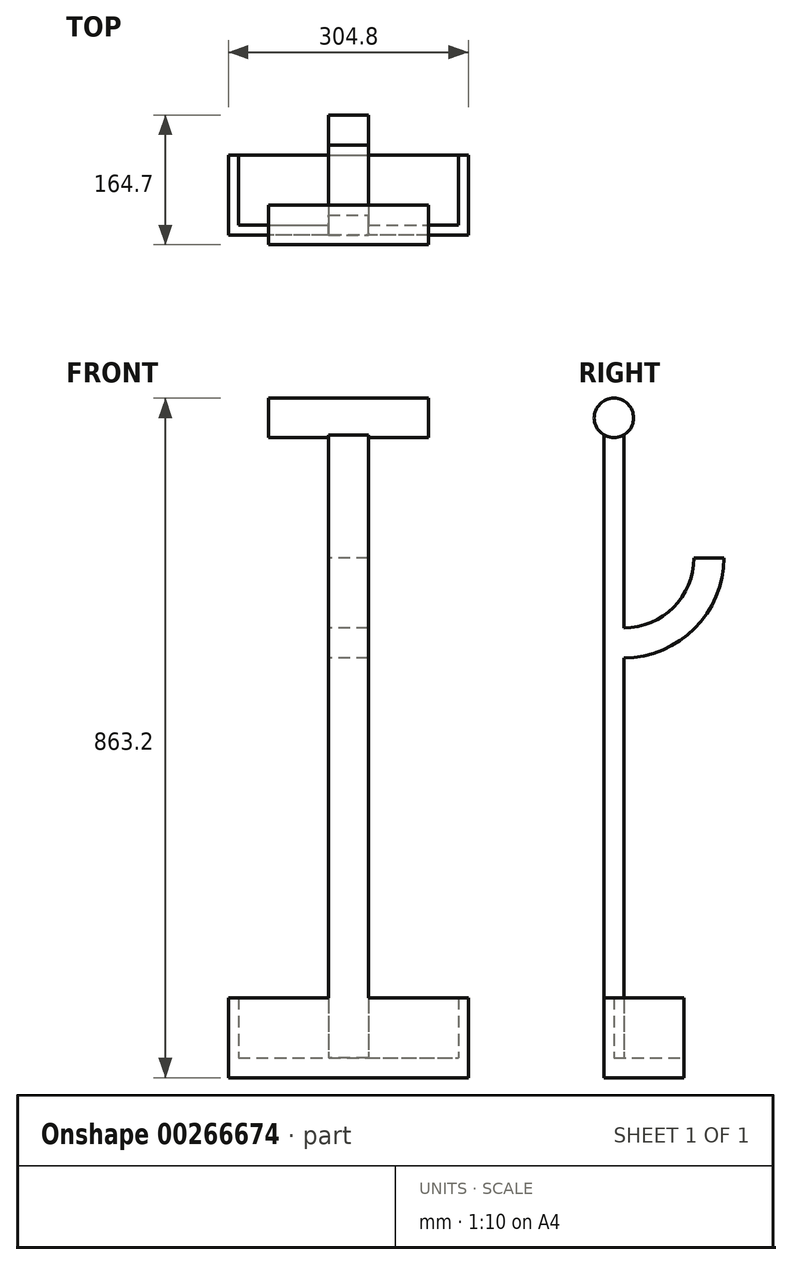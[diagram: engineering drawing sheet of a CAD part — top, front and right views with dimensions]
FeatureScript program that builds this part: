
annotation { "Feature Type Name" : "Feature", "Feature Type Description" : "" }
export const myFeature = defineFeature(function(context is Context, id is Id, definition is map)
    precondition{}
    {
        {
            var Q0;
            Q0=qCreatedBy(makeId("Top.planeOp"),FACE);
            var sketch = newSketch(context, id + "F0", { "sketchPlane" : qUnion([Q0])});
            skLineSegment(sketch, "E0", {"start": v(0, 0) * mm, "end": v(-152.4, 0) * mm});
            skLineSegment(sketch, "E1", {"start": v(-152.4, 0) * mm, "end": v(-152.4, 101.6) * mm});
            skLineSegment(sketch, "E2", {"start": v(-152.4, 101.6) * mm, "end": v(152.4, 101.6) * mm});
            skLineSegment(sketch, "E3", {"start": v(152.4, 101.6) * mm, "end": v(152.4, 0) * mm});
            skLineSegment(sketch, "E4", {"start": v(152.4, 0) * mm, "end": v(0, 0) * mm});
            skLineSegment(sketch, "E5", {"start": v(25.4, 0) * mm, "end": v(25.4, 25.4) * mm});
            skLineSegment(sketch, "E6", {"start": v(25.4, 25.4) * mm, "end": v(-25.4, 25.4) * mm});
            skLineSegment(sketch, "E7", {"start": v(-25.4, 25.4) * mm, "end": v(-25.4, 0) * mm});
            skLineSegment(sketch, "E8", {"start": v(-139.7, 101.6) * mm, "end": v(-139.7, 12.7) * mm});
            skLineSegment(sketch, "E9", {"start": v(-139.7, 12.7) * mm, "end": v(-25.4, 12.7) * mm});
            skLineSegment(sketch, "E10", {"start": v(25.4, 12.7) * mm, "end": v(139.7, 12.7) * mm});
            skLineSegment(sketch, "E11", {"start": v(139.7, 12.7) * mm, "end": v(139.7, 101.6) * mm});
            skSolve(sketch);
        }
        {
            var Q0;
            {var subQ1=sQuery(id+"F0.wireOp",EDGE,"E6");Q0=makeQuery(id+"F0.imprint","IMPRINT",FACE,{"disambiguationData":[TD([[makeQuery(id+"F0.imprint","IMPRINT",EDGE,{"derivedFrom":subQ1}),-1.0]])]});}
            extrude(context, id + "F1", {"entities" : qUnion([Q0]), "depth" : 25.4 * mm});
        }
        {
            var Q0;
            {var subQ5=sQuery(id+"F0.wireOp",EDGE,"E1");Q0=makeQuery(id+"F0.imprint","IMPRINT",FACE,{"disambiguationData":[TD([[makeQuery(id+"F0.imprint","IMPRINT",EDGE,{"derivedFrom":subQ5}),-1.0]])]});}
            var Q1;
            {var subQ4=sQuery(id+"F0.wireOp",EDGE,"E3");Q1=makeQuery(id+"F0.imprint","IMPRINT",FACE,{"disambiguationData":[TD([[makeQuery(id+"F0.imprint","IMPRINT",EDGE,{"derivedFrom":subQ4}),-1.0]])]});}
            extrude(context, id + "F2", {"entities" : qUnion([Q0, Q1]), "operationType" : NewBodyOperationType.ADD, "depth" : 101.6 * mm});
        }
        {
            var Q0;
            {var subQ0=sQuery(id+"F0.wireOp",EDGE,"E6");Q0=makeQuery(id+"F0.imprint","IMPRINT",FACE,{"disambiguationData":[TD([[makeQuery(id+"F0.imprint","IMPRINT",EDGE,{"derivedFrom":subQ0}),1.0]])]});}
            extrude(context, id + "F3", {"entities" : qUnion([Q0]), "operationType" : NewBodyOperationType.ADD, "depth" : 838.2 * mm});
        }
        {
            var Q0;
            Q0=makeQuery(id+"F3.opExtrude","SWEPT_FACE",FACE,{"disambiguationData":[OSD([sQuery(id+"F0.wireOp",EDGE,"E7")])]});
            var sketch = newSketch(context, id + "F4", { "sketchPlane" : qUnion([Q0])});
            skCircle(sketch, "E12", {"center": v(-12.7, 838.2) * mm, "radius": 25 * mm});
            skArc(sketch, "E13", {"start": v(-114.3, 660.4) * mm, "mid": v(-88.26, 597.54) * mm, "end": v(-25.4, 571.5) * mm});
            skPoint(sketch, "E14", {"position": v(-25.4, 838.2) * mm});
            skArc(sketch, "E15.0", {"start": v(-152.4, 660.4) * mm, "mid": v(-115.2, 570.6) * mm, "end": v(-25.4, 533.4) * mm});
            skLineSegment(sketch, "E16", {"start": v(-152.4, 660.4) * mm, "end": v(-114.3, 660.4) * mm});
            skLineSegment(sketch, "E17", {"start": v(-114.3, 660.4) * mm, "end": v(-25.4, 660.4) * mm, "construction": true});
            skSolve(sketch);
        }
        {
            var Q0;
            {var subQ0=sQuery(id+"F4.wireOp",EDGE,"E13");Q0=makeQuery(id+"F4.imprint","IMPRINT",FACE,{"disambiguationData":[TD([[makeQuery(id+"F4.imprint","IMPRINT",EDGE,{"derivedFrom":subQ0}),-1.0]])]});}
            extrude(context, id + "F5", {"entities" : qUnion([Q0]), "operationType" : NewBodyOperationType.ADD, "oppositeDirection" : true, "depth" : 50.8 * mm});
        }
        {
            var Q0;
            {var subQ1=sQuery(id+"F0.wireOp",EDGE,"E7");var subQ6=makeQuery(id+"F3.opExtrude","CAP_EDGE",EDGE,{"disambiguationData":[OSD([subQ1])],"isStart":false});Q0=makeQuery(id+"F4.imprint","IMPRINT",FACE,{"disambiguationData":[TD([[makeQuery(id+"F4.imprint","IMPRINT",EDGE,{"derivedFrom":subQ6}),1.0]])]});}
            var Q1;
            {var subQ1=sQuery(id+"F0.wireOp",EDGE,"E7");var subQ6=makeQuery(id+"F3.opExtrude","CAP_EDGE",EDGE,{"disambiguationData":[OSD([subQ1])],"isStart":false});Q1=makeQuery(id+"F4.imprint","IMPRINT",FACE,{"disambiguationData":[TD([[makeQuery(id+"F4.imprint","IMPRINT",EDGE,{"derivedFrom":subQ6}),-1.0]])]});}
            extrude(context, id + "F6", {"entities" : qUnion([Q0, Q1]), "depth" : 76.2 * mm});
        }
        {
            var Q0;
            Q0=makeQuery(id+"F6.opExtrude","CAP_FACE",FACE,{"disambiguationData":[OSD([sQuery(id+"F0.wireOp",EDGE,"E0"),sQuery(id+"F0.wireOp",EDGE,"E6"),sQuery(id+"F0.wireOp",EDGE,"E7"),sQuery(id+"F4.wireOp",EDGE,"E12")])],"isStart":true});
            extrude(context, id + "F7", {"entities" : qUnion([Q0]), "operationType" : NewBodyOperationType.ADD, "depth" : 127 * mm});
        }
    });
